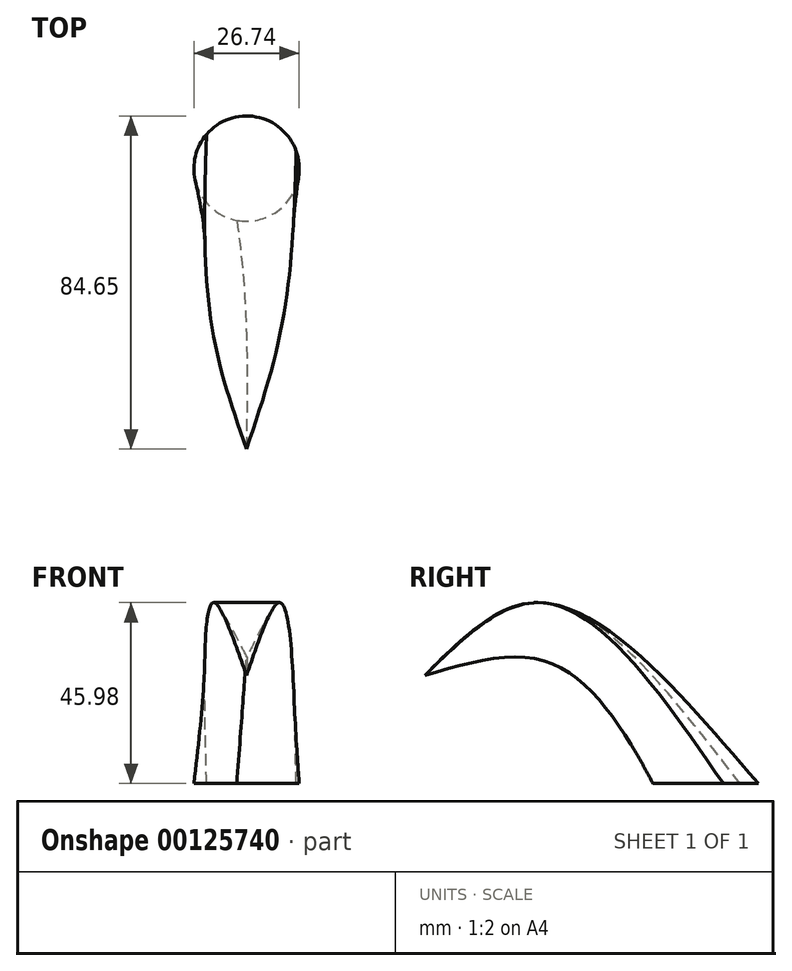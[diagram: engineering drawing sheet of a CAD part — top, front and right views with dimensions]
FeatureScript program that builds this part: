
annotation { "Feature Type Name" : "Feature", "Feature Type Description" : "" }
export const myFeature = defineFeature(function(context is Context, id is Id, definition is map)
    precondition{}
    {
        {
            var Q0;
            Q0=qCreatedBy(makeId("Top.planeOp"),FACE);
            var Q1;
            Q1=qCreatedBy(makeId("Front.planeOp"),FACE);
            cPlane(context, id + "F0", {"entities" : qUnion([Q0, Q1]), "cplaneType" : CPlaneType.MID_PLANE, "offset" : 25.4 * mm, "width" : 152.4 * mm, "height" : 152.4 * mm});
        }
        {
            var Q0;
            Q0=qCreatedBy(makeId("Top.planeOp"),FACE);
            var sketch = newSketch(context, id + "F1", { "sketchPlane" : qUnion([Q0])});
            skCircle(sketch, "E0", {"center": v(0, 43.75) * mm, "radius": 13.37 * mm});
            skSolve(sketch);
        }
        {
            var Q0;
            Q0=qCreatedBy(makeId("Front.planeOp"),FACE);
            var sketch = newSketch(context, id + "F2", { "sketchPlane" : qUnion([Q0])});
            skCircle(sketch, "E1.cCircle", {"center": v(0, 41.24) * mm, "radius": 4.71 * mm, "construction": true});
            skLineSegment(sketch, "E1.0", {"start": v(-8.16, 45.95) * mm, "end": v(8.16, 45.95) * mm});
            skLineSegment(sketch, "E1.1", {"start": v(8.16, 45.95) * mm, "end": v(0, 31.82) * mm});
            skLineSegment(sketch, "E1.2", {"start": v(0, 31.82) * mm, "end": v(-8.16, 45.95) * mm});
            skPoint(sketch, "E1.0.midPoint", {"position": v(0, 45.95) * mm});
            skSolve(sketch);
        }
        {
            var Q0;
            Q0=qCreatedBy(id+"F0.planeOp",FACE);
            var sketch = newSketch(context, id + "F3", { "sketchPlane" : qUnion([Q0])});
            skCircle(sketch, "E2", {"center": v(0, 38.94) * mm, "radius": 5.97 * mm});
            skSolve(sketch);
        }
        {
            var Q0;
            Q0=makeQuery(id+"F1.imprint","IMPRINT",FACE,{"disambiguationData":[TD([[makeQuery(id+"F1.imprint","IMPRINT",EDGE,{"derivedFrom":sQuery(id+"F1.wireOp",EDGE,"E0")}),1.0]])]});
            var Q1;
            Q1=makeQuery(id+"F2.imprint","IMPRINT",FACE,{"disambiguationData":[TD([[makeQuery(id+"F2.imprint","IMPRINT",EDGE,{"derivedFrom":sQuery(id+"F2.wireOp",EDGE,"E1.0")}),-1.0]])]});
            var Q2;
            Q2=sQuery(id+"F3.wireOp",VERTEX,"E2.center");
            loft(context, id + "F4", {"sheetProfilesArray" : [{ "sheetProfileEntities" : qUnion([Q0]) }, { "sheetProfileEntities" : qUnion([Q1]) }, { "sheetProfileEntities" : qUnion([Q2]) }]});
        }
    });
